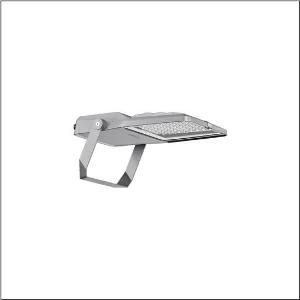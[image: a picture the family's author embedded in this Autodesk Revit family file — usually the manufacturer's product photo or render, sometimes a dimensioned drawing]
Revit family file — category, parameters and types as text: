
# Revit family: floodlight_fl_21_iq_mini___rs12_5xa7771d4b1a_77d6
name_source: partatom
category: Lighting Fixtures
units: mm (PartAtom-declared; Revit-internal decimal feet)

## family parameters
Cut with Voids When Loaded = No
Host = Face
Light Source = No
Part Type = Normal
Room Calculation Point = No
Round Connector Dimension = Use Diameter
Shared = No

## types (1)
- --- (1 x LED, 18810 lm, 143 W, 4000K)
    Apparent Load = 143 VA
    CIE Flux Codes = 79 92 99 100 100
    Color Rendering = 70
    Color Temperature = 4000K
    Default Elevation = 1800 mm
    Description = Floodlight FL 21 iQ mini, floodlight, primary light control with lens, of PMMA, primary optical cover: protective disc, of toughened safety glass, transparent, light distribution: RS12, light emission: direct distribution, installation type: surface-mounted, LED, High Power LED, rated luminous flux: 18.810lm, luminous efficacy: 132lm/W, light colour: 740, colour temperature: 4000K, control: Auto-Match, Temp-Guard, Lumen-Switch, Night-Set, Smart-Wire, Light-Fading, Desk-Remote (wireless, voltage-free reading and setting of iQ features in the workshop via application-optimized NFC function/RFID function), optimised constant luminous flux control (CLO 2.0), with terminal, 6-pole, mains connection: 220..240V, AC, 50/60Hz, start of lifetime: 143W, end of service life: 152W, reduction: 61W, luminaire housing, of diecast aluminium, powder-coated, Siteco® metallic grey (DB 702S), corrosivity category C5 mid according to DIN EN ISO 12944, sealing non-destructively replaceable, mounting bracket, of steel, galvanised, powder-coated, Siteco® metallic grey (DB 702S), protection rating (complete): IP66, insulation class (complete): insulation class II (safety insulation), certification: CE, ENEC, VDE, protection symbol: D, impact resistance: IK08, permissible operating ambient temperature: -40..+40°C, permissible operating ambient temperature for outdoor applications: -40..+50°C, standard: DIN EN 12944, LABS conformity tested according to VDMA 24364:2018-05, packaging unit: 1 piece

Light Distribution: RS12
    Height = 70 mm
    Lamp = 1 x LED
    Lamp Light Flux = 18810 lm
    Lamp Power = 143 W
    Lamp count = 1
    Length = 485 mm
    Luminous efficacy = 132 lm/W
    Manufacturer = Siteco
    ModVariant = No
    Model = 5XA7771D4B1A
    Number of Poles = 1
    OnlyDefault = Yes
    Power Factor = 1
    Product Name = Floodlight FL 21 iQ mini | RS12
    Product group = floodlight | pylon annexe
    ProductGroupID = 6200
    Protection Class = Protection class II
    Protection Degree = IP 66
    RLX_Detail_Level = 1
    RLX_Emergency_Light_Flux = 0 lm
    RLX_Emergency_Type = 0
    RLX_Emergency_Type_DB = No
    RlxData = <blob elided: 91369 chars, md5=a3451cf4>
    Socket = socket
    Standby Power = 0 W
    System Light Flux = 18810 lm
    System Power = 143 W
    Type Comments = factory setting: luminous flux: 100 % | dim-lin: 254 | 730 mA
    Type Image = l_1006845.jpg
    URL = http://relux.com
    VarID = @adj_099767
    Voltage = 0 V
    Weight = 0.00 kg
    Width = 337 mm

## geometry (parser evidence)
native form markers: Blend x4, Sweep x13
no freeform markers — native parametric forms only
